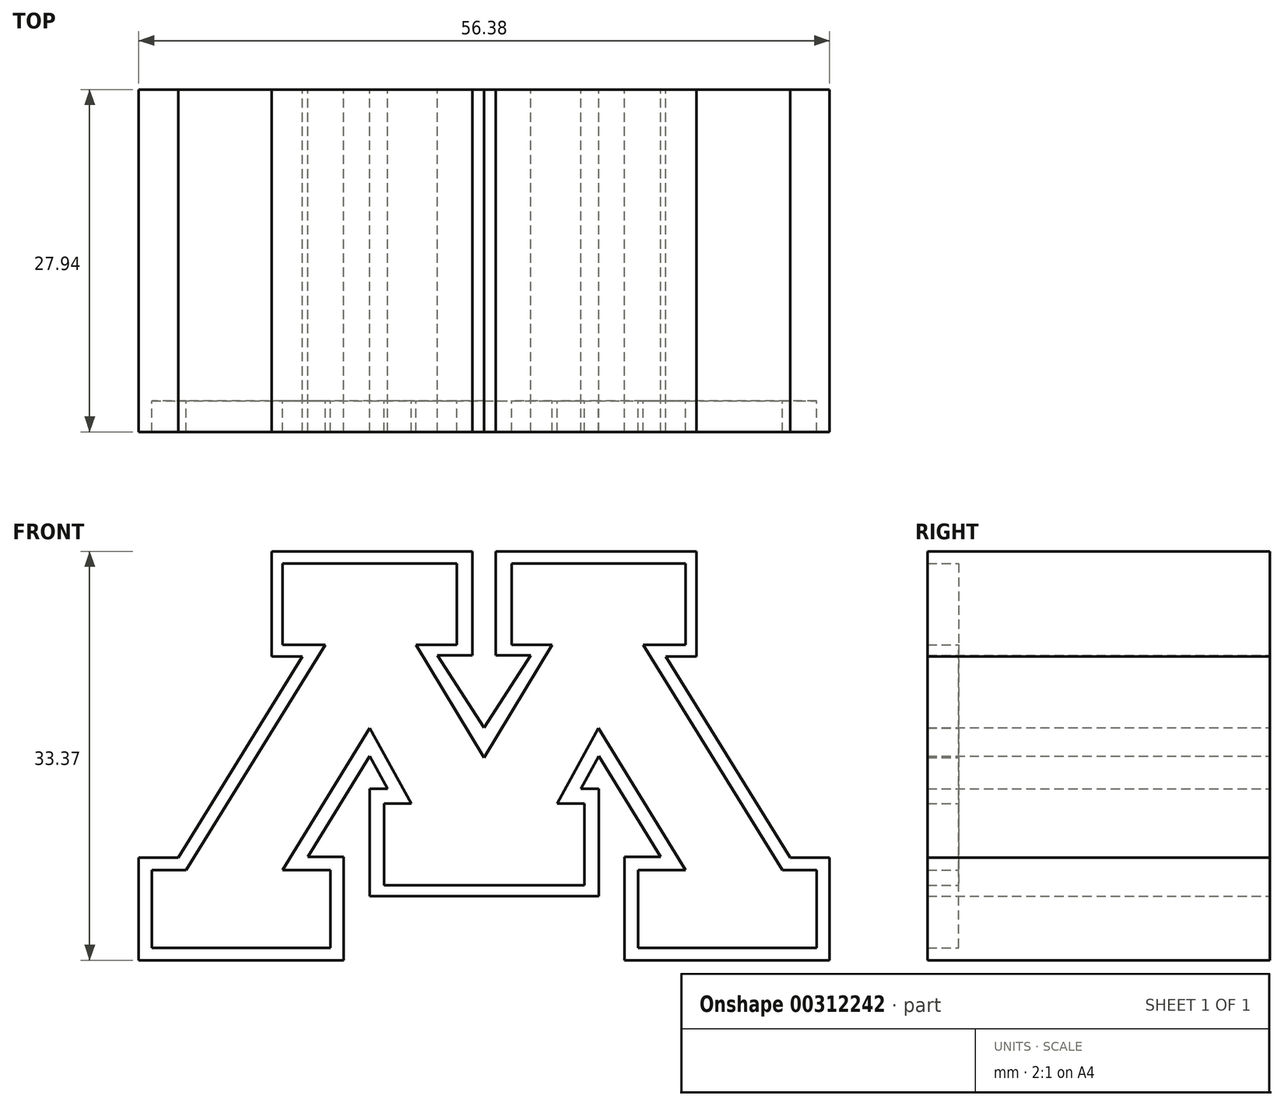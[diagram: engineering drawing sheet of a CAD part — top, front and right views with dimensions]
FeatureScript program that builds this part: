
annotation { "Feature Type Name" : "Feature", "Feature Type Description" : "" }
export const myFeature = defineFeature(function(context is Context, id is Id, definition is map)
    precondition{}
    {
        {
            var Q0;
            Q0=qCreatedBy(makeId("Front.planeOp"),FACE);
            var sketch = newSketch(context, id + "F0", { "sketchPlane" : qUnion([Q0])});
            skLineSegment(sketch, "E0", {"start": v(0, 39.68) * mm, "end": v(-3.81, 45.59) * mm});
            skLineSegment(sketch, "E1", {"start": v(-3.81, 45.59) * mm, "end": v(-0.96, 45.59) * mm});
            skLineSegment(sketch, "E2", {"start": v(-0.96, 45.59) * mm, "end": v(-0.96, 54.08) * mm});
            skLineSegment(sketch, "E3", {"start": v(-0.96, 54.08) * mm, "end": v(-17.34, 54.08) * mm});
            skLineSegment(sketch, "E4", {"start": v(-17.34, 54.08) * mm, "end": v(-17.34, 45.48) * mm});
            skLineSegment(sketch, "E5", {"start": v(-17.34, 45.48) * mm, "end": v(-14.83, 45.48) * mm});
            skLineSegment(sketch, "E6", {"start": v(-14.83, 45.48) * mm, "end": v(-24.98, 29.08) * mm});
            skLineSegment(sketch, "E7", {"start": v(-24.98, 29.08) * mm, "end": v(-28.19, 29.08) * mm});
            skLineSegment(sketch, "E8", {"start": v(-28.19, 29.08) * mm, "end": v(-28.19, 20.7) * mm});
            skLineSegment(sketch, "E9", {"start": v(-28.19, 20.7) * mm, "end": v(-11.46, 20.7) * mm});
            skLineSegment(sketch, "E10", {"start": v(-11.46, 20.7) * mm, "end": v(-11.46, 29.13) * mm});
            skLineSegment(sketch, "E11", {"start": v(-11.46, 29.13) * mm, "end": v(-14.4, 29.13) * mm});
            skLineSegment(sketch, "E12", {"start": v(-14.4, 29.13) * mm, "end": v(-9.35, 37.36) * mm});
            skLineSegment(sketch, "E13", {"start": v(-9.35, 37.36) * mm, "end": v(-7.9, 34.71) * mm});
            skLineSegment(sketch, "E14", {"start": v(-7.9, 34.71) * mm, "end": v(-9.35, 34.71) * mm});
            skLineSegment(sketch, "E15", {"start": v(-9.35, 34.71) * mm, "end": v(-9.35, 25.93) * mm});
            skLineSegment(sketch, "E16", {"start": v(-9.35, 25.93) * mm, "end": v(0, 25.93) * mm});
            skLineSegment(sketch, "E17", {"start": v(0, 25.93) * mm, "end": v(0, 39.68) * mm});
            skLineSegment(sketch, "E18", {"start": v(0, 37.23) * mm, "end": v(-5.56, 46.44) * mm});
            skLineSegment(sketch, "E19", {"start": v(-5.56, 46.44) * mm, "end": v(-2.24, 46.44) * mm});
            skLineSegment(sketch, "E20", {"start": v(-2.24, 46.44) * mm, "end": v(-2.24, 53.1) * mm});
            skLineSegment(sketch, "E21", {"start": v(-2.24, 53.1) * mm, "end": v(-16.44, 53.1) * mm});
            skLineSegment(sketch, "E22", {"start": v(-16.44, 53.1) * mm, "end": v(-16.44, 46.44) * mm});
            skLineSegment(sketch, "E23", {"start": v(-16.44, 46.44) * mm, "end": v(-12.98, 46.44) * mm});
            skLineSegment(sketch, "E24", {"start": v(-12.98, 46.44) * mm, "end": v(-24.34, 28.07) * mm});
            skLineSegment(sketch, "E25", {"start": v(-24.34, 28.07) * mm, "end": v(-27.13, 28.07) * mm});
            skLineSegment(sketch, "E26", {"start": v(-27.13, 28.07) * mm, "end": v(-27.13, 21.73) * mm});
            skLineSegment(sketch, "E27", {"start": v(-27.13, 21.73) * mm, "end": v(-12.55, 21.73) * mm});
            skLineSegment(sketch, "E28", {"start": v(-12.55, 21.73) * mm, "end": v(-12.55, 28.07) * mm});
            skLineSegment(sketch, "E29", {"start": v(-12.55, 28.07) * mm, "end": v(-16.44, 28.07) * mm});
            skLineSegment(sketch, "E30", {"start": v(-16.44, 28.07) * mm, "end": v(-9.34, 39.66) * mm});
            skLineSegment(sketch, "E31", {"start": v(-9.34, 39.66) * mm, "end": v(-5.95, 33.5) * mm});
            skLineSegment(sketch, "E32", {"start": v(-5.95, 33.5) * mm, "end": v(-8.18, 33.5) * mm});
            skLineSegment(sketch, "E33", {"start": v(-8.18, 33.5) * mm, "end": v(-8.18, 26.83) * mm});
            skLineSegment(sketch, "E34", {"start": v(-8.18, 26.83) * mm, "end": v(0, 26.83) * mm});
            skSolve(sketch);
        }
        {
            var Q0;
            {var subQ0=sQuery(id+"F0.wireOp",EDGE,"E18");Q0=makeQuery(id+"F0.imprint","IMPRINT",FACE,{"disambiguationData":[TD([[makeQuery(id+"F0.imprint","IMPRINT",EDGE,{"derivedFrom":subQ0}),1.0]])]});}
            extrude(context, id + "F1", {"entities" : qUnion([Q0]), "depth" : 25.4 * mm});
        }
        {
            var Q0;
            {var subQ2=sQuery(id+"F0.wireOp",EDGE,"E0");Q0=makeQuery(id+"F0.imprint","IMPRINT",FACE,{"disambiguationData":[TD([[makeQuery(id+"F0.imprint","IMPRINT",EDGE,{"derivedFrom":subQ2}),1.0]])]});}
            extrude(context, id + "F2", {"entities" : qUnion([Q0]), "operationType" : NewBodyOperationType.ADD, "depth" : 27.94 * mm});
        }
        {
            var Q0;
            Q0=makeQuery(id+"F1.opExtrude","SWEPT_BODY",BODY,{"disambiguationData":[OSD([sQuery(id+"F0.wireOp",EDGE,"E17"),sQuery(id+"F0.wireOp",EDGE,"E18"),sQuery(id+"F0.wireOp",EDGE,"E19"),sQuery(id+"F0.wireOp",EDGE,"E20"),sQuery(id+"F0.wireOp",EDGE,"E21"),sQuery(id+"F0.wireOp",EDGE,"E22"),sQuery(id+"F0.wireOp",EDGE,"E23"),sQuery(id+"F0.wireOp",EDGE,"E24"),sQuery(id+"F0.wireOp",EDGE,"E25"),sQuery(id+"F0.wireOp",EDGE,"E26"),sQuery(id+"F0.wireOp",EDGE,"E27"),sQuery(id+"F0.wireOp",EDGE,"E28"),sQuery(id+"F0.wireOp",EDGE,"E29"),sQuery(id+"F0.wireOp",EDGE,"E30"),sQuery(id+"F0.wireOp",EDGE,"E31"),sQuery(id+"F0.wireOp",EDGE,"E32"),sQuery(id+"F0.wireOp",EDGE,"E33"),sQuery(id+"F0.wireOp",EDGE,"E34")])]});
            var Q1;
            {var subQ0=sQuery(id+"F0.wireOp",EDGE,"E17");Q1=makeQuery(id+"F2.boolean.opBoolean","MERGE",FACE,{"derivedFrom":[makeQuery(id+"F1.opExtrude","SWEPT_FACE",FACE,{"disambiguationData":[OSD([subQ0])]}),makeQuery(id+"F2.opExtrude","SWEPT_FACE",FACE,{"disambiguationData":[OSD([subQ0]),TDD([makeQuery(id+"F0.imprint","IMPRINT",EDGE,{"disambiguationData":[TD([[makeQuery(id+"F0.imprint","INTERSECT",VERTEX,{"derivedFrom":[sQuery(id+"F0.wireOp",EDGE,"E16"),subQ0]}),-1.0]])],"derivedFrom":subQ0})])]}),makeQuery(id+"F2.opExtrude","SWEPT_FACE",FACE,{"disambiguationData":[OSD([subQ0]),TDD([makeQuery(id+"F0.imprint","IMPRINT",EDGE,{"disambiguationData":[TD([[makeQuery(id+"F0.imprint","INTERSECT",VERTEX,{"derivedFrom":[sQuery(id+"F0.wireOp",EDGE,"E0"),subQ0]}),1.0]])],"derivedFrom":subQ0})])]})]});}
            mirror(context, id + "F3", {"operationType" : NewBodyOperationType.ADD, "entities" : qUnion([Q0]), "mirrorPlane" : qUnion([Q1])});
        }
    });
